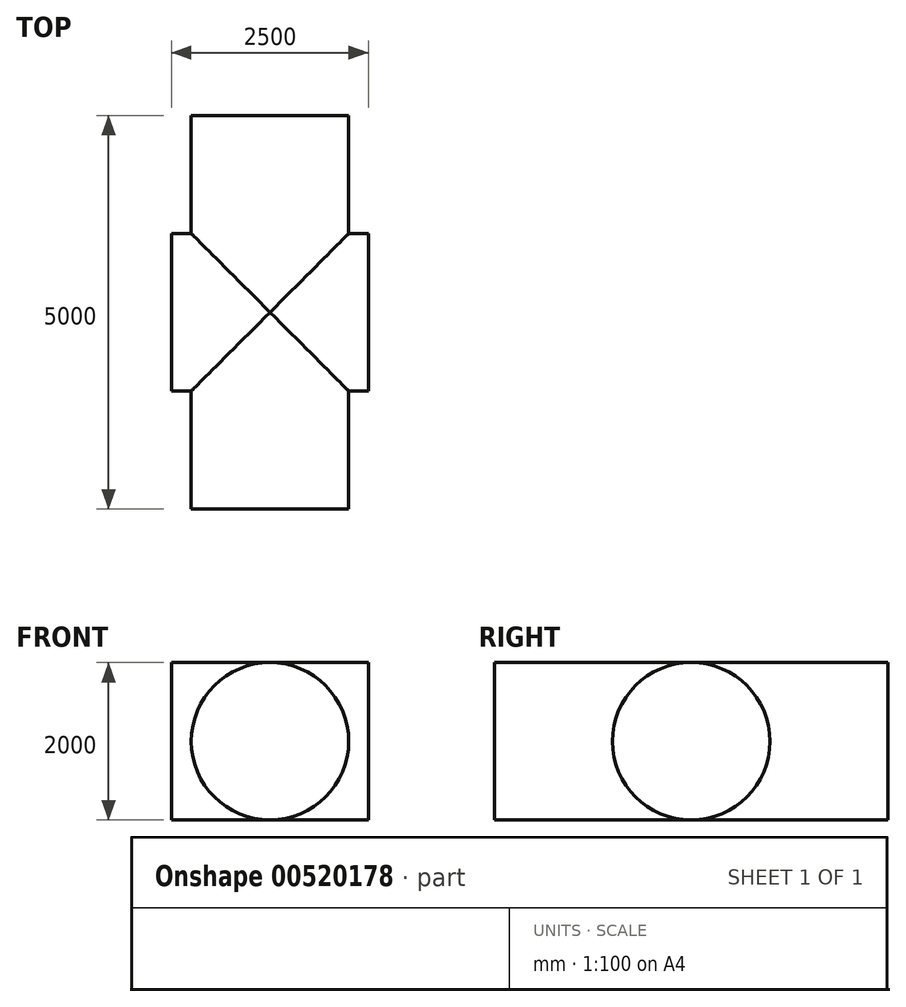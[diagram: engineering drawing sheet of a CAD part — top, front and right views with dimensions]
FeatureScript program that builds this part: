
annotation { "Feature Type Name" : "Feature", "Feature Type Description" : "" }
export const myFeature = defineFeature(function(context is Context, id is Id, definition is map)
    precondition{}
    {
        {
            var Q0;
            Q0=qCreatedBy(makeId("Front.planeOp"),FACE);
            var sketch = newSketch(context, id + "F0", { "sketchPlane" : qUnion([Q0])});
            skCircle(sketch, "E0", {"center": v(0, 0) * mm, "radius": 1000 * mm});
            skSolve(sketch);
        }
        {
            var Q0;
            Q0=qCreatedBy(makeId("Right.planeOp"),FACE);
            var sketch = newSketch(context, id + "F1", { "sketchPlane" : qUnion([Q0])});
            skCircle(sketch, "E1", {"center": v(0, 0) * mm, "radius": 1000 * mm});
            skSolve(sketch);
        }
        {
            var Q0;
            Q0=makeQuery(id+"F0.imprint","IMPRINT",FACE,{"disambiguationData":[TD([[makeQuery(id+"F0.imprint","IMPRINT",EDGE,{"derivedFrom":sQuery(id+"F0.wireOp",EDGE,"E0")}),1.0]])]});
            extrude(context, id + "F2", {"entities" : qUnion([Q0]), "endBound" : BoundingType.SYMMETRIC, "depth" : 5000 * mm, "offsetDistance" : 25 * mm});
        }
        {
            var Q0;
            Q0 = qSketchRegion(id + "F1", true);
            extrude(context, id + "F3", {"entities" : qUnion([Q0]), "operationType" : NewBodyOperationType.ADD, "endBound" : BoundingType.SYMMETRIC, "depth" : 2500 * mm, "offsetDistance" : 25 * mm});
        }
    });
